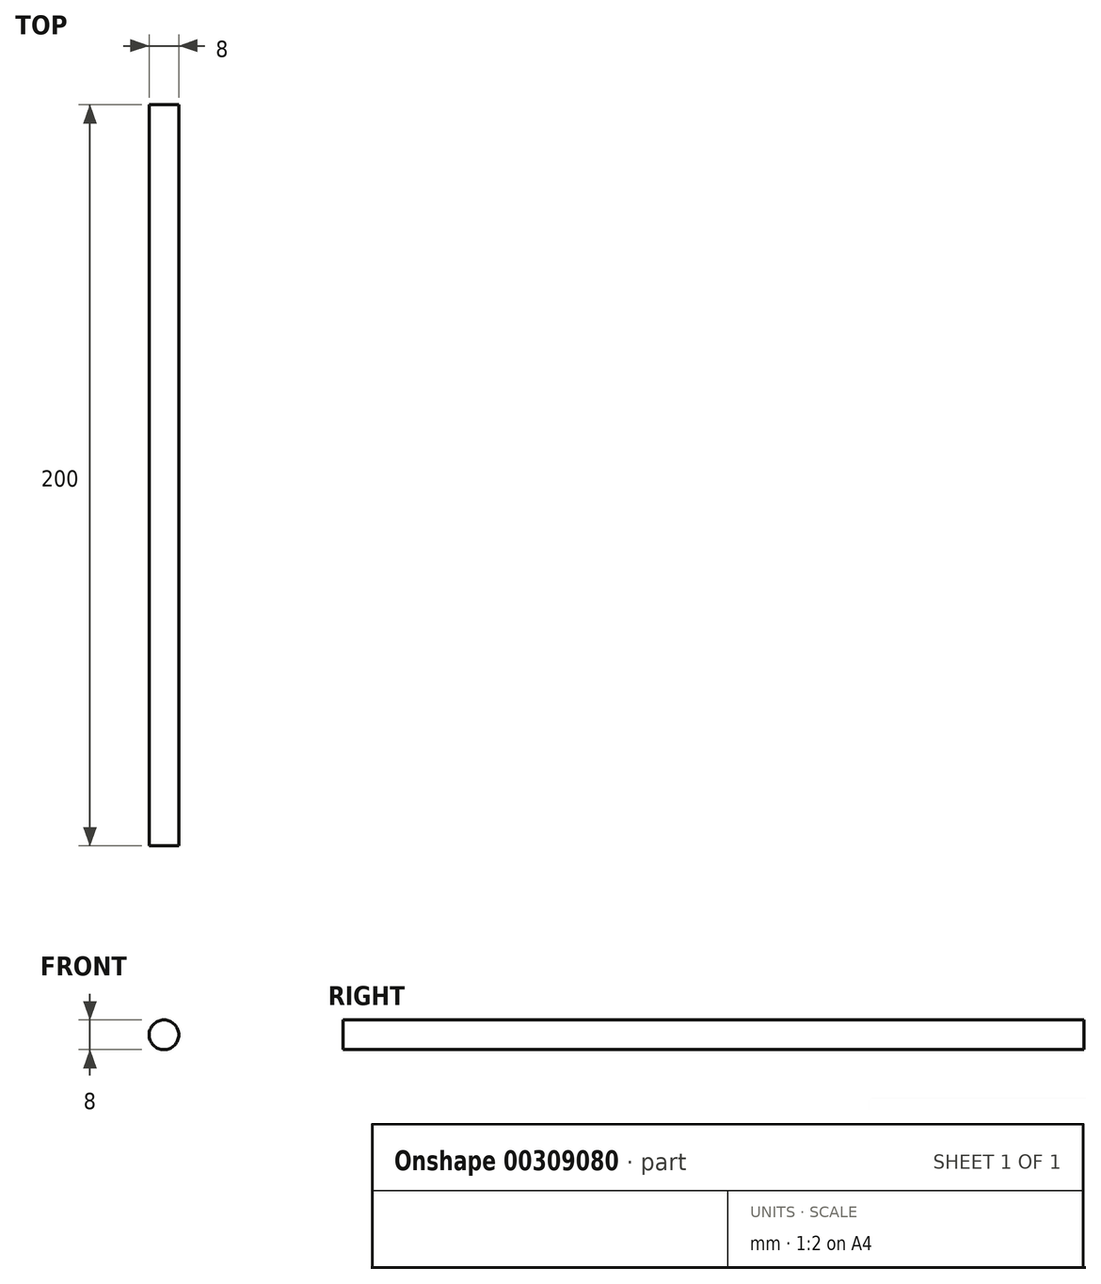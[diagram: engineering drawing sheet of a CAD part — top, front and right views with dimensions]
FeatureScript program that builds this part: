
annotation { "Feature Type Name" : "Feature", "Feature Type Description" : "" }
export const myFeature = defineFeature(function(context is Context, id is Id, definition is map)
    precondition{}
    {
        {
            var Q0;
            Q0=qCreatedBy(makeId("Front.planeOp"),FACE);
            var sketch = newSketch(context, id + "F0", { "sketchPlane" : qUnion([Q0])});
            skCircle(sketch, "E0", {"center": v(0, 0) * mm, "radius": 4 * mm});
            skSolve(sketch);
        }
        {
            var Q0;
            Q0 = qSketchRegion(id + "F0", true);
            extrude(context, id + "F1", {"entities" : qUnion([Q0]), "depth" : 200 * mm});
        }
    });
